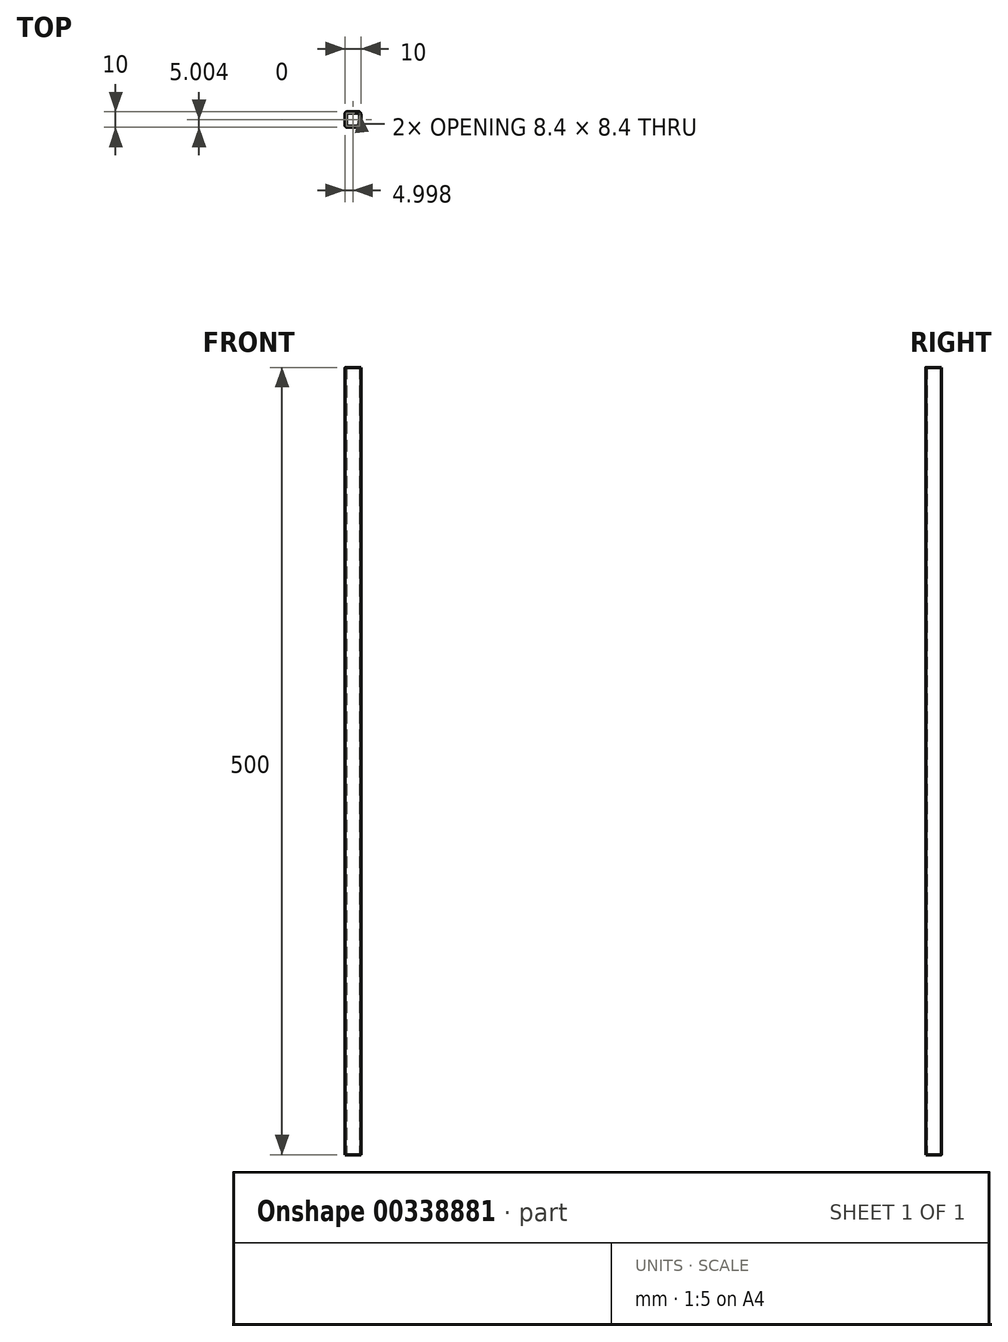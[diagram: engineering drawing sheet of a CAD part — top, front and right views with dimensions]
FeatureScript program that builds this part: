
annotation { "Feature Type Name" : "Feature", "Feature Type Description" : "" }
export const myFeature = defineFeature(function(context is Context, id is Id, definition is map)
    precondition{}
    {
        {
            var Q0;
            Q0=qCreatedBy(makeId("Top.planeOp"),FACE);
            var sketch = newSketch(context, id + "F0", { "sketchPlane" : qUnion([Q0])});
            skLineSegment(sketch, "E0.bottom", {"start": v(-18.32, 28.81) * mm, "end": v(-11.28, 28.81) * mm});
            skLineSegment(sketch, "E0.top", {"start": v(-18.32, 18.81) * mm, "end": v(-11.28, 18.81) * mm});
            skLineSegment(sketch, "E0.left", {"start": v(-19.8, 27.34) * mm, "end": v(-19.8, 20.3) * mm});
            skLineSegment(sketch, "E0.right", {"start": v(-9.8, 27.34) * mm, "end": v(-9.8, 20.3) * mm});
            skLineSegment(sketch, "E1.0", {"start": v(-17.52, 28.01) * mm, "end": v(-12.08, 28.01) * mm});
            skLineSegment(sketch, "E1.1", {"start": v(-19, 26.54) * mm, "end": v(-19, 21.1) * mm});
            skLineSegment(sketch, "E1.2", {"start": v(-17.52, 19.61) * mm, "end": v(-12.08, 19.61) * mm});
            skLineSegment(sketch, "E1.3", {"start": v(-10.6, 26.54) * mm, "end": v(-10.6, 21.1) * mm});
            skPoint(sketch, "E2.visualSharp", {"position": v(-19.8, 28.81) * mm});
            skArc(sketch, "E2.filletArc", {"start": v(-18.32, 28.81) * mm, "mid": v(-19.37, 28.38) * mm, "end": v(-19.8, 27.34) * mm});
            skPoint(sketch, "E3.visualSharp", {"position": v(-19, 28.01) * mm});
            skArc(sketch, "E3.filletArc", {"start": v(-17.52, 28.01) * mm, "mid": v(-18.57, 27.58) * mm, "end": v(-19, 26.54) * mm});
            skPoint(sketch, "E4.visualSharp", {"position": v(-9.8, 28.81) * mm});
            skArc(sketch, "E4.filletArc", {"start": v(-9.8, 27.34) * mm, "mid": v(-10.23, 28.38) * mm, "end": v(-11.28, 28.81) * mm});
            skPoint(sketch, "E5.visualSharp", {"position": v(-10.6, 28.01) * mm});
            skArc(sketch, "E5.filletArc", {"start": v(-10.6, 26.54) * mm, "mid": v(-11.03, 27.58) * mm, "end": v(-12.08, 28.01) * mm});
            skPoint(sketch, "E6.visualSharp", {"position": v(-10.6, 19.61) * mm});
            skArc(sketch, "E6.filletArc", {"start": v(-12.08, 19.61) * mm, "mid": v(-11.03, 20.05) * mm, "end": v(-10.6, 21.1) * mm});
            skPoint(sketch, "E7.visualSharp", {"position": v(-19, 19.61) * mm});
            skArc(sketch, "E7.filletArc", {"start": v(-19, 21.1) * mm, "mid": v(-18.57, 20.05) * mm, "end": v(-17.52, 19.61) * mm});
            skPoint(sketch, "E8.visualSharp", {"position": v(-9.8, 18.81) * mm});
            skArc(sketch, "E8.filletArc", {"start": v(-11.28, 18.81) * mm, "mid": v(-10.23, 19.25) * mm, "end": v(-9.8, 20.3) * mm});
            skArc(sketch, "E9.filletArc", {"start": v(-19.8, 20.3) * mm, "mid": v(-19.37, 19.25) * mm, "end": v(-18.32, 18.81) * mm});
            skSolve(sketch);
        }
        {
            var Q0;
            Q0=makeQuery(id+"F0.imprint","IMPRINT",FACE,{"disambiguationData":[TD([[makeQuery(id+"F0.imprint","IMPRINT",EDGE,{"derivedFrom":sQuery(id+"F0.wireOp",EDGE,"E0.bottom")}),-1.0]])]});
            extrude(context, id + "F1", {"entities" : qUnion([Q0]), "depth" : 500 * mm});
        }
        {
            var Q0;
            Q0=makeQuery(id+"F0.imprint","IMPRINT",FACE,{"disambiguationData":[TD([[makeQuery(id+"F0.imprint","IMPRINT",EDGE,{"derivedFrom":sQuery(id+"F0.wireOp",EDGE,"E0.bottom")}),-1.0]])]});
            extrude(context, id + "F2", {"entities" : qUnion([Q0]), "depth" : 500 * mm});
        }
    });
